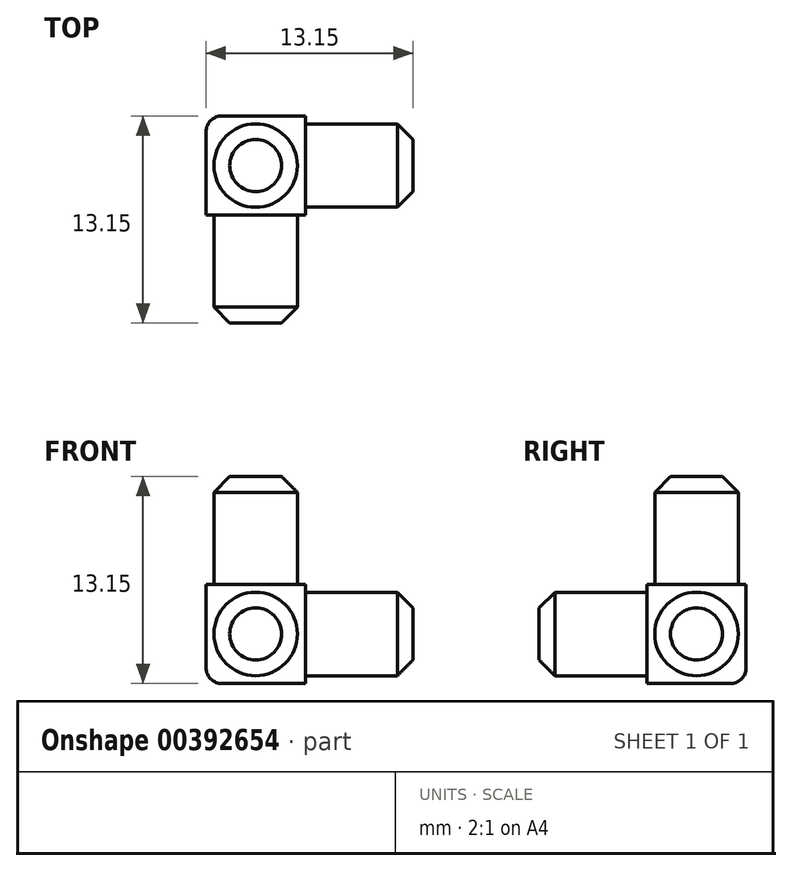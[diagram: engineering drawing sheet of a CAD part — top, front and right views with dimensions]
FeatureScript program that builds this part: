
annotation { "Feature Type Name" : "Feature", "Feature Type Description" : "" }
export const myFeature = defineFeature(function(context is Context, id is Id, definition is map)
    precondition{}
    {
        {
            assignVariable(context, id + "F0", {"name" : "Diameter", "anyValue" : 5.3});
        }
        {
            assignVariable(context, id + "F1", {"name" : "Length", "anyValue" : 10});
        }
        {
            var Q0;
            Q0=qCreatedBy(makeId("Front.planeOp"),FACE);
            var sketch = newSketch(context, id + "F2", { "sketchPlane" : qUnion([Q0])});
            skCircle(sketch, "E0", {"center": v(0, 0) * mm, "radius": 2.65 * mm});
            skSolve(sketch);
        }
        {
            var Q0;
            Q0=qCreatedBy(makeId("Right.planeOp"),FACE);
            var sketch = newSketch(context, id + "F3", { "sketchPlane" : qUnion([Q0])});
            skCircle(sketch, "E1", {"center": v(0, 0) * mm, "radius": 2.65 * mm});
            skSolve(sketch);
        }
        {
            var Q0;
            Q0=qCreatedBy(makeId("Top.planeOp"),FACE);
            var sketch = newSketch(context, id + "F4", { "sketchPlane" : qUnion([Q0])});
            skCircle(sketch, "E2", {"center": v(0, 0) * mm, "radius": 2.65 * mm});
            skSolve(sketch);
        }
        {
            var Q0;
            Q0=makeQuery(id+"F2.imprint","IMPRINT",FACE,{"disambiguationData":[TD([[makeQuery(id+"F2.imprint","IMPRINT",EDGE,{"derivedFrom":sQuery(id+"F2.wireOp",EDGE,"E0")}),1.0]])]});
            extrude(context, id + "F5", {"entities" : qUnion([Q0]), "depth" : (getVariable(context, 'Length')) * mm});
        }
        {
            var Q0;
            Q0=makeQuery(id+"F4.imprint","IMPRINT",FACE,{"disambiguationData":[TD([[makeQuery(id+"F4.imprint","IMPRINT",EDGE,{"derivedFrom":sQuery(id+"F4.wireOp",EDGE,"E2")}),1.0]])]});
            extrude(context, id + "F6", {"entities" : qUnion([Q0]), "operationType" : NewBodyOperationType.ADD, "depth" : (getVariable(context, 'Length')) * mm});
        }
        {
            var Q0;
            Q0=makeQuery(id+"F3.imprint","IMPRINT",FACE,{"disambiguationData":[TD([[makeQuery(id+"F3.imprint","IMPRINT",EDGE,{"derivedFrom":sQuery(id+"F3.wireOp",EDGE,"E1")}),1.0]])]});
            extrude(context, id + "F7", {"entities" : qUnion([Q0]), "operationType" : NewBodyOperationType.ADD, "depth" : (getVariable(context, 'Length')) * mm});
        }
        {
            var Q0;
            Q0=makeQuery(id+"F6.opExtrude","CAP_FACE",FACE,{"disambiguationData":[OSD([sQuery(id+"F4.wireOp",EDGE,"E2")])],"isStart":true});
            var sketch = newSketch(context, id + "F8", { "sketchPlane" : qUnion([Q0])});
            skLineSegment(sketch, "E3.bottom", {"start": v(-3.15, -3.15) * mm, "end": v(3.15, -3.15) * mm});
            skLineSegment(sketch, "E3.top", {"start": v(-3.15, 3.15) * mm, "end": v(3.15, 3.15) * mm});
            skLineSegment(sketch, "E3.left", {"start": v(-3.15, -3.15) * mm, "end": v(-3.15, 3.15) * mm});
            skLineSegment(sketch, "E3.right", {"start": v(3.15, -3.15) * mm, "end": v(3.15, 3.15) * mm});
            skPoint(sketch, "E3.middle", {"position": v(0, 0) * mm});
            skSolve(sketch);
        }
        {
            var Q0;
            {var subQ6=sQuery(id+"F8.wireOp",EDGE,"E3.top");Q0=makeQuery(id+"F8.imprint","IMPRINT",FACE,{"disambiguationData":[TD([[makeQuery(id+"F8.imprint","IMPRINT",EDGE,{"derivedFrom":subQ6}),-1.0]])]});}
            var Q1;
            {var subQ0=sQuery(id+"F4.wireOp",EDGE,"E2");Q1=makeQuery(id+"F8.imprint","IMPRINT",FACE,{"disambiguationData":[TD([[makeQuery(id+"F8.imprint","IMPRINT",EDGE,{"derivedFrom":makeQuery(id+"F6.opExtrude","CAP_EDGE",EDGE,{"disambiguationData":[OSD([subQ0])],"isStart":true})}),-1.0]])]});}
            var Q2;
            {var subQ1=sQuery(id+"F4.wireOp",EDGE,"E2");var subQ3=makeQuery(id+"F6.opExtrude","CAP_EDGE",EDGE,{"disambiguationData":[OSD([subQ1])],"isStart":true});Q2=makeQuery(id+"F8.imprint","IMPRINT",FACE,{"disambiguationData":[TD([[makeQuery(id+"F8.imprint","IMPRINT",EDGE,{"derivedFrom":subQ3}),1.0]])]});}
            extrude(context, id + "F9", {"entities" : qUnion([Q0, Q1, Q2]), "operationType" : NewBodyOperationType.ADD, "endBound" : BoundingType.SYMMETRIC, "depth" : (getVariable(context, 'Diameter') + 1) * mm});
        }
        {
            var Q0;
            Q0=makeQuery(id+"F9.opExtrude","CAP_EDGE",EDGE,{"disambiguationData":[OSD([sQuery(id+"F8.wireOp",EDGE,"E3.bottom")])],"isStart":false});
            var Q1;
            Q1=makeQuery(id+"F9.opExtrude","SWEPT_EDGE",EDGE,{"disambiguationData":[OSD([sQuery(id+"F8.wireOp",EDGE,"E3.bottom"),sQuery(id+"F8.wireOp",EDGE,"E3.left")])]});
            var Q2;
            Q2=makeQuery(id+"F9.opExtrude","CAP_EDGE",EDGE,{"disambiguationData":[OSD([sQuery(id+"F8.wireOp",EDGE,"E3.left")])],"isStart":false});
            fillet(context, id + "F10", {"entities" : qUnion([Q0, Q1, Q2]), "radius" : 1 * mm, "tangentPropagation" : true, "allowEdgeOverflow" : false});
        }
        {
            var Q0;
            Q0=makeQuery(id+"F7.opExtrude","CAP_EDGE",EDGE,{"disambiguationData":[OSD([sQuery(id+"F3.wireOp",EDGE,"E1")])],"isStart":false});
            var Q1;
            Q1=makeQuery(id+"F6.opExtrude","CAP_EDGE",EDGE,{"disambiguationData":[OSD([sQuery(id+"F4.wireOp",EDGE,"E2")])],"isStart":false});
            var Q2;
            Q2=makeQuery(id+"F5.opExtrude","CAP_EDGE",EDGE,{"disambiguationData":[OSD([sQuery(id+"F2.wireOp",EDGE,"E0")])],"isStart":false});
            chamfer(context, id + "F11", {"entities" : qUnion([Q0, Q1, Q2]), "width" : 1 * mm, "tangentPropagation" : true});
        }
    });
